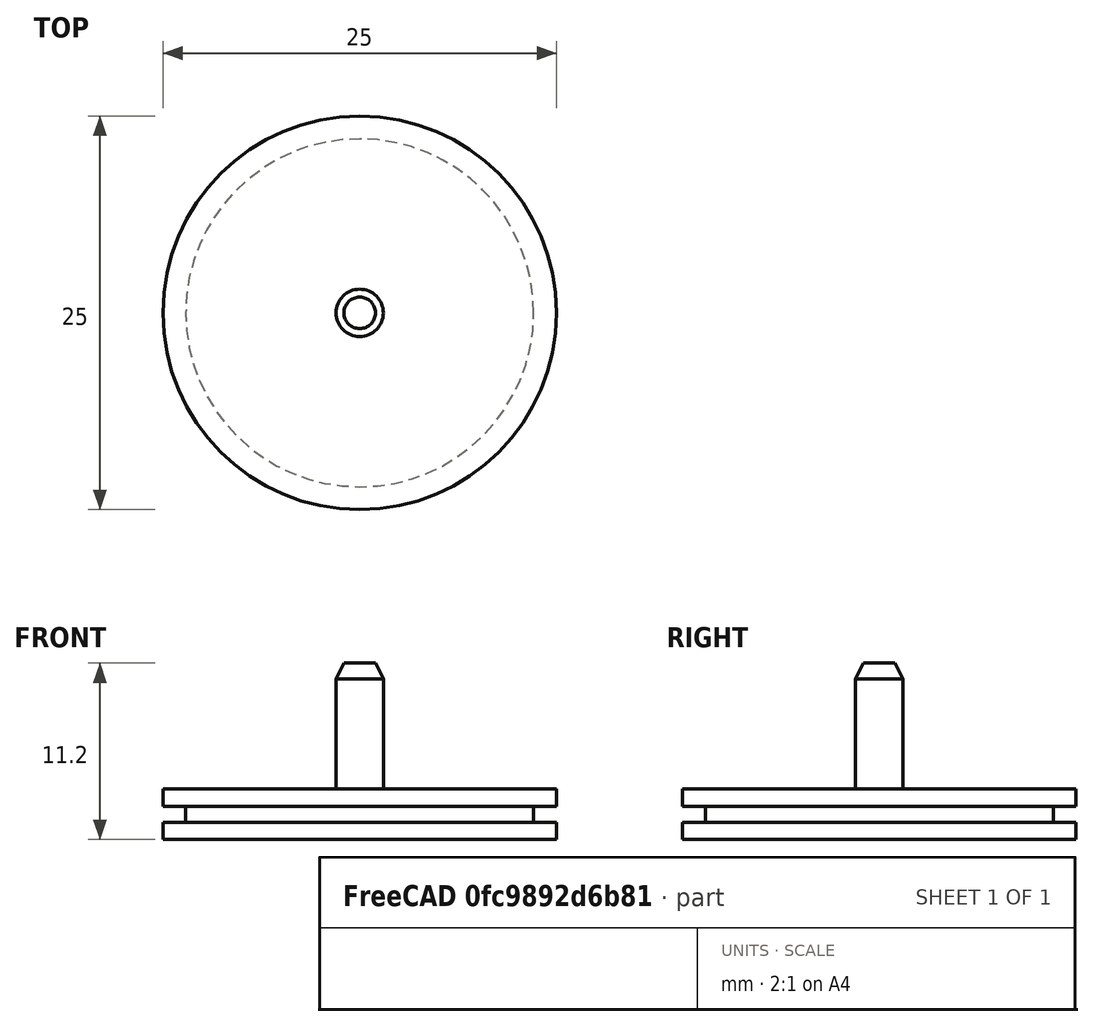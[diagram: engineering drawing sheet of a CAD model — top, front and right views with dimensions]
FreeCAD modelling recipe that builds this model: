
FCSTD DOCUMENT  (FreeCAD 0.20R29603 (Git))
Label: SampleHolderLarge01
License: All rights reserved
LicenseURL: http://en.wikipedia.org/wiki/All_rights_reserved
objects: TechDraw::DrawViewDimension×9, Part::Cylinder×4, Part::MultiFuse×2, Part::Cone×1, Part::Feature×1, TechDraw::DrawSVGTemplate×1, TechDraw::DrawProjGroupItem×1, TechDraw::DrawProjGroup×1, TechDraw::DrawViewPart×1, TechDraw::DrawViewAnnotation×1, TechDraw::DrawPage×1
note: 8 computed .brp shape members not serialized (recipe doc carries the construction recipe); baked Part::Feature solids carry a one-line shape summary decoded from their .brp

FEATURE [Part::Cylinder] Cylinder  label="Zylinder"
  Angle = 360
  AttacherType = Attacher::AttachEngine3D
  FirstAngle = 0
  Height = 10.2
  Radius = 1.5
  SecondAngle = 0
FEATURE [Part::Cylinder] Cylinder001  label="Zylinder001"
  Angle = 360
  AttacherType = Attacher::AttachEngine3D
  FirstAngle = 0
  Height = 1.1
  Radius = 12.5
  SecondAngle = 0
FEATURE [Part::Cylinder] Cylinder002  label="Zylinder002"
  Angle = 360
  AttacherType = Attacher::AttachEngine3D
  FirstAngle = 0
  Height = 1.1
  Placement = pos=(0,0,2.1) rot=(0,0,1;0rad)
  Radius = 12.5
  SecondAngle = 0
FEATURE [Part::Cylinder] Cylinder003  label="Zylinder003"
  Angle = 360
  AttacherType = Attacher::AttachEngine3D
  FirstAngle = 0
  Height = 1
  Placement = pos=(0,0,1.1) rot=(0,0,1;0rad)
  Radius = 11.05
  SecondAngle = 0
FEATURE [Part::MultiFuse] Fusion
  Shapes = -> [Cylinder,Cylinder001,Cylinder002,Cylinder003]
FEATURE [Part::Cone] Cone  label="Kegel"
  Angle = 360
  AttacherType = Attacher::AttachEngine3D
  Height = 1
  Placement = pos=(0,0,10.2) rot=(0,0,1;0rad)
  Radius1 = 1.5
  Radius2 = 1
FEATURE [Part::MultiFuse] Fusion001
  Shapes = -> [Fusion,Cone]
FEATURE [Part::Feature] Fusion001_solid  label="SampleHolderLarge01"
  shape: bbox 25 x 25 x 11.2 mm, 11 faces (baked)
FEATURE [TechDraw::DrawSVGTemplate] Template
  EditableTexts = Designed_by_Name=Thomas Spielauer; FC-Date=2023-07-12; FC-SC=mm; FC-SH=01; FC-Title=Large simple sampleholder; Subtitle=For FEGSEM Quanta 250
  Height = 210
  Orientation = 1
  Width = 297
FEATURE [TechDraw::DrawProjGroupItem] ProjItem
  CoarseView = false
  Direction = (0,1,0)
  Focus = 100
  HardHidden = false
  IsoCount = 0
  IsoHidden = false
  IsoVisible = false
  LockPosition = true
  Perspective = false
  Rotation = 0
  RotationVector = (1,0,0)
  Scale = 5
  ScaleType = 2
  SeamHidden = false
  SeamVisible = true
  SmoothHidden = false
  SmoothVisible = true
  Source = -> [Fusion001_solid]
  Type = 0
  X = 0
  XDirection = (1,0,0)
  Y = 0
FEATURE [TechDraw::DrawProjGroup] ProjGroup
  Anchor = -> ProjItem
  AutoDistribute = false
  LockPosition = false
  ProjectionType = 0
  Rotation = 0
  Scale = 5
  ScaleType = 2
  Source = -> [Fusion001_solid]
  Views = -> [ProjItem]
  X = 139.923
  Y = 135.325
  spacingX = 15
  spacingY = 15
FEATURE [TechDraw::DrawViewDimension] Dimension
  AngleOverride = false
  Arbitrary = false
  ArbitraryTolerances = false
  EqualTolerance = true
  ExtensionAngle = 0
  FormatSpec = %.2w
  FormatSpecOverTolerance = %+.2w
  FormatSpecUnderTolerance = %+.2w
  Inverted = false
  LineAngle = 0
  LockPosition = false
  MeasureType = 1
  OverTolerance = 0
  References2D = -> [ProjItem]
  Rotation = 0
  ScaleType = 0
  TheoreticalExact = false
  Type = 0
  UnderTolerance = 0
  X = 15.5918
  Y = -30.4792
FEATURE [TechDraw::DrawViewDimension] Dimension001
  AngleOverride = false
  Arbitrary = false
  ArbitraryTolerances = false
  EqualTolerance = true
  ExtensionAngle = 0
  FormatSpec = %.2w
  FormatSpecOverTolerance = %+.2w
  FormatSpecUnderTolerance = %+.2w
  Inverted = false
  LineAngle = 0
  LockPosition = false
  MeasureType = 1
  OverTolerance = 0
  References2D = -> [ProjItem]
  Rotation = 0
  ScaleType = 0
  TheoreticalExact = false
  Type = 0
  UnderTolerance = 0
  X = 16.1568
  Y = -39.0244
FEATURE [TechDraw::DrawViewDimension] Dimension002
  AngleOverride = false
  Arbitrary = false
  ArbitraryTolerances = false
  EqualTolerance = true
  ExtensionAngle = 0
  FormatSpec = %.2w
  FormatSpecOverTolerance = %+.2w
  FormatSpecUnderTolerance = %+.2w
  Inverted = false
  LineAngle = 0
  LockPosition = false
  MeasureType = 1
  OverTolerance = 0
  References2D = -> [ProjItem]
  Rotation = 0
  ScaleType = 0
  TheoreticalExact = false
  Type = 0
  UnderTolerance = 0
  X = 70.3166
  Y = -22.3352
FEATURE [TechDraw::DrawViewDimension] Dimension003
  AngleOverride = false
  Arbitrary = false
  ArbitraryTolerances = false
  EqualTolerance = true
  ExtensionAngle = 0
  FormatSpec = %.2w
  FormatSpecOverTolerance = %+.2w
  FormatSpecUnderTolerance = %+.2w
  Inverted = false
  LineAngle = 0
  LockPosition = false
  MeasureType = 1
  OverTolerance = 0
  References2D = -> [ProjItem]
  Rotation = 0
  ScaleType = 0
  TheoreticalExact = false
  Type = 0
  UnderTolerance = 0
  X = 73.0678
  Y = 1.90267
FEATURE [TechDraw::DrawViewDimension] Dimension004
  AngleOverride = false
  Arbitrary = false
  ArbitraryTolerances = false
  EqualTolerance = true
  ExtensionAngle = 0
  FormatSpec = %.2w
  FormatSpecOverTolerance = %+.2w
  FormatSpecUnderTolerance = %+.2w
  Inverted = false
  LineAngle = 0
  LockPosition = false
  MeasureType = 1
  OverTolerance = 0
  References2D = -> [ProjItem]
  Rotation = 0
  ScaleType = 0
  TheoreticalExact = false
  Type = 0
  UnderTolerance = 0
  X = 88.6709
  Y = 8.34021
FEATURE [TechDraw::DrawViewDimension] Dimension005
  AngleOverride = false
  Arbitrary = false
  ArbitraryTolerances = false
  EqualTolerance = true
  ExtensionAngle = 0
  FormatSpec = %.2w
  FormatSpecOverTolerance = %+.2w
  FormatSpecUnderTolerance = %+.2w
  Inverted = false
  LineAngle = 0
  LockPosition = false
  MeasureType = 1
  OverTolerance = 0
  References2D = -> [ProjItem]
  Rotation = 0
  ScaleType = 0
  TheoreticalExact = false
  Type = 0
  UnderTolerance = 0
  X = 91.81
  Y = 35.0071
FEATURE [TechDraw::DrawViewDimension] Dimension006
  AngleOverride = false
  Arbitrary = false
  ArbitraryTolerances = false
  EqualTolerance = true
  ExtensionAngle = 0
  FormatSpec = %.2w
  FormatSpecOverTolerance = %+.2w
  FormatSpecUnderTolerance = %+.2w
  Inverted = false
  LineAngle = 0
  LockPosition = false
  MeasureType = 1
  OverTolerance = 0
  References2D = -> [ProjItem]
  Rotation = 0
  ScaleType = 0
  TheoreticalExact = false
  Type = 0
  UnderTolerance = 0
  X = 106.878
  Y = 15.0028
FEATURE [TechDraw::DrawViewDimension] Dimension007
  AngleOverride = false
  Arbitrary = false
  ArbitraryTolerances = false
  EqualTolerance = true
  ExtensionAngle = 0
  FormatSpec = %.2w
  FormatSpecOverTolerance = %+.2w
  FormatSpecUnderTolerance = %+.2w
  Inverted = false
  LineAngle = 0
  LockPosition = false
  MeasureType = 1
  OverTolerance = 0
  References2D = -> [ProjItem]
  Rotation = 0
  ScaleType = 0
  TheoreticalExact = false
  Type = 0
  UnderTolerance = 0
  X = -3.20574
  Y = 60.5224
FEATURE [TechDraw::DrawViewDimension] Dimension008
  AngleOverride = false
  Arbitrary = false
  ArbitraryTolerances = false
  EqualTolerance = true
  ExtensionAngle = 0
  FormatSpec = %.2w
  FormatSpecOverTolerance = %+.2w
  FormatSpecUnderTolerance = %+.2w
  Inverted = false
  LineAngle = 0
  LockPosition = false
  MeasureType = 1
  OverTolerance = 0
  References2D = -> [ProjItem]
  Rotation = 0
  ScaleType = 0
  TheoreticalExact = false
  Type = 0
  UnderTolerance = 0
  X = -2.30165
  Y = 52.8101
FEATURE [TechDraw::DrawViewPart] View
  CoarseView = false
  Direction = (-0.532,-0.795,0.293)
  Focus = 100
  HardHidden = false
  IsoCount = 0
  IsoHidden = false
  IsoVisible = false
  LockPosition = false
  Perspective = false
  Rotation = 0
  ScaleType = 0
  SeamHidden = false
  SeamVisible = true
  SmoothHidden = false
  SmoothVisible = true
  Source = -> [Fusion001_solid]
  X = 42.8226
  XDirection = (-0.673,0.607,0.423)
  Y = 156.769
FEATURE [TechDraw::DrawViewAnnotation] Annotation
  Font = osifont
  LineSpace = 80
  LockPosition = false
  MaxWidth = -1
  Rotation = 0
  ScaleType = 0
  Text = Note: Do not build mandril screwed into the sample holder, always turn out of full material (vibrational damping!)
  TextSize = 5
  TextStyle = 0
  X = 148.175
  Y = 66.5943
FEATURE [TechDraw::DrawPage] Page
  KeepUpdated = true
  NextBalloonIndex = 1
  ProjectionType = 0
  Template = -> Template
  Views = -> [ProjGroup,Dimension,Dimension001,Dimension002,Dimension003,Dimension004,Dimension005,Dimension006,Dimension007,Dimension008,View,Annotation]
